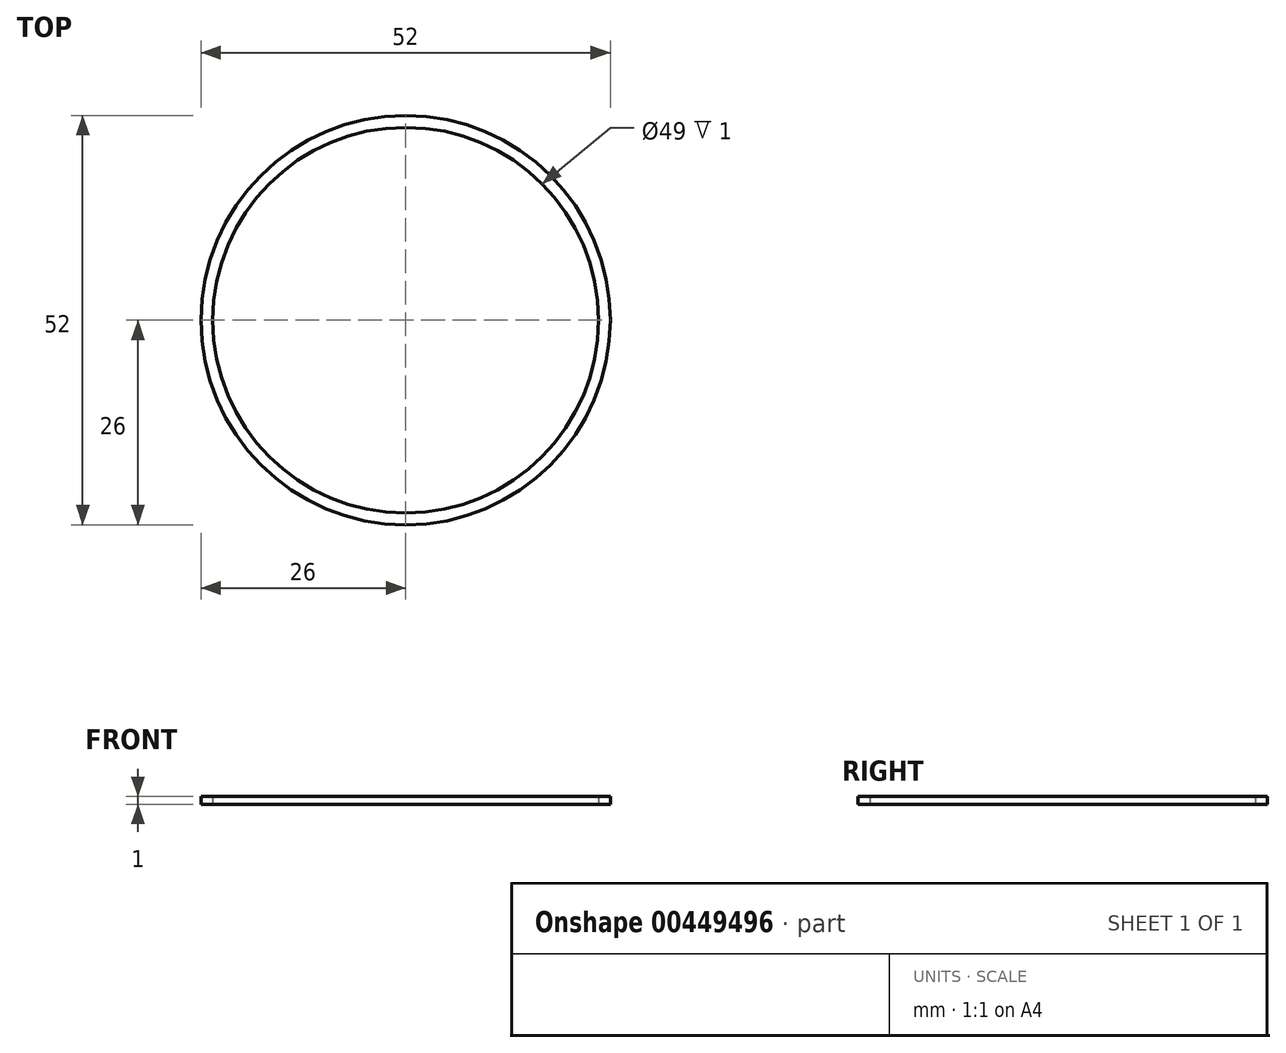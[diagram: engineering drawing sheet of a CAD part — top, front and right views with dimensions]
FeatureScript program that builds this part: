
annotation { "Feature Type Name" : "Feature", "Feature Type Description" : "" }
export const myFeature = defineFeature(function(context is Context, id is Id, definition is map)
    precondition{}
    {
        {
            var Q0;
            Q0=qCreatedBy(makeId("Top.planeOp"),FACE);
            var sketch = newSketch(context, id + "F0", { "sketchPlane" : qUnion([Q0])});
            skCircle(sketch, "E0", {"center": v(0, 0) * mm, "radius": 26 * mm});
            skCircle(sketch, "E1", {"center": v(0, 0) * mm, "radius": 24.5 * mm});
            skSolve(sketch);
        }
        {
            var Q0;
            Q0=makeQuery(id+"F0.imprint","IMPRINT",FACE,{"disambiguationData":[TD([[makeQuery(id+"F0.imprint","IMPRINT",EDGE,{"derivedFrom":sQuery(id+"F0.wireOp",EDGE,"E0")}),1.0]])]});
            extrude(context, id + "F1", {"entities" : qUnion([Q0]), "depth" : 1 * mm});
        }
    });
